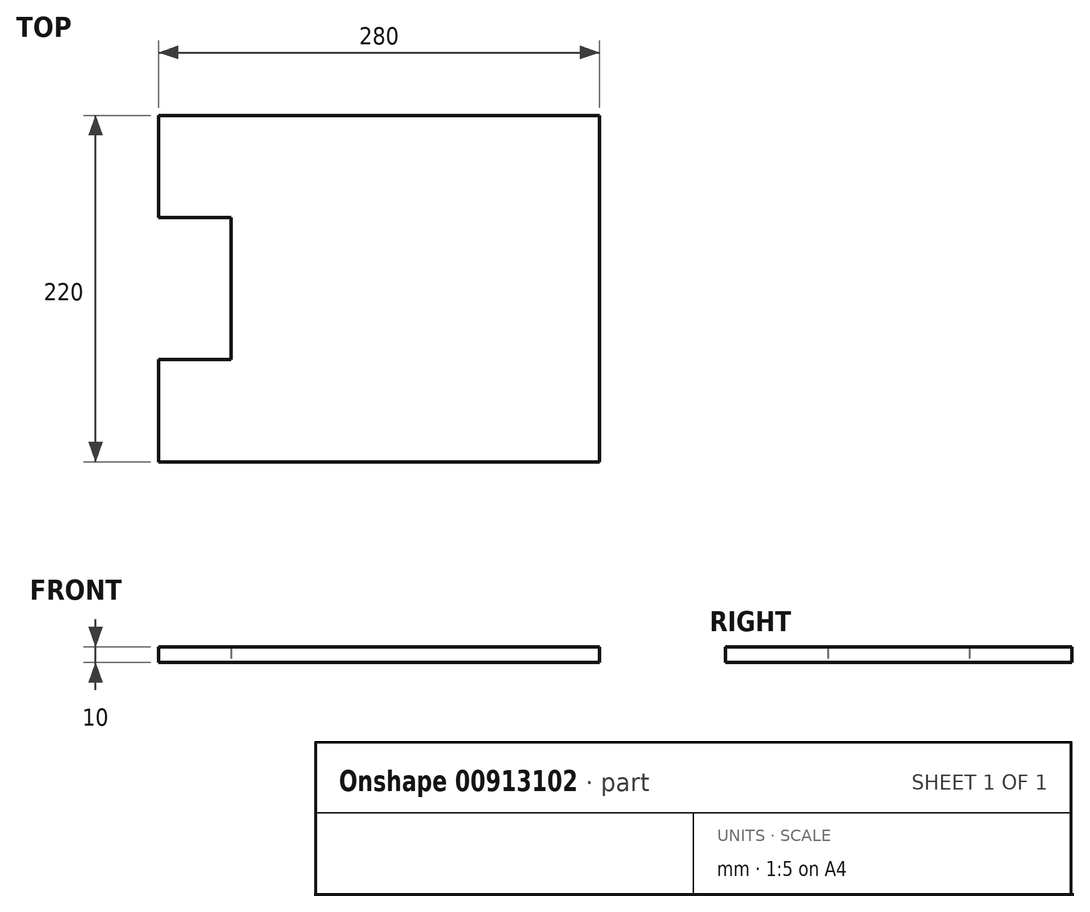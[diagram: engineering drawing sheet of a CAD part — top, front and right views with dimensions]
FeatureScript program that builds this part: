
annotation { "Feature Type Name" : "Feature", "Feature Type Description" : "" }
export const myFeature = defineFeature(function(context is Context, id is Id, definition is map)
    precondition{}
    {
        {
            var Q0;
            Q0=qCreatedBy(makeId("Top.planeOp"),FACE);
            var sketch = newSketch(context, id + "F0", { "sketchPlane" : qUnion([Q0])});
            skLineSegment(sketch, "E0.bottom", {"start": v(140, -110) * mm, "end": v(-140, -110) * mm});
            skLineSegment(sketch, "E0.top", {"start": v(140, 110) * mm, "end": v(-140, 110) * mm});
            skLineSegment(sketch, "E0.left", {"start": v(140, -110) * mm, "end": v(140, 110) * mm});
            skPoint(sketch, "E0.middle", {"position": v(0, 0) * mm});
            skLineSegment(sketch, "E1", {"start": v(-140, 110) * mm, "end": v(-140, 45) * mm});
            skLineSegment(sketch, "E2.MirrorCS", {"start": v(-140, -110) * mm, "end": v(-140, -45) * mm});
            skLineSegment(sketch, "E3", {"start": v(-140, 45) * mm, "end": v(-93.91, 45) * mm});
            skLineSegment(sketch, "E4.MirrorCS", {"start": v(-140, -45) * mm, "end": v(-93.91, -45) * mm});
            skLineSegment(sketch, "E5", {"start": v(-93.91, 45) * mm, "end": v(-93.91, -45) * mm});
            skSolve(sketch);
        }
        {
            var Q0;
            Q0 = qSketchRegion(id + "F0", true);
            extrude(context, id + "F1", {"entities" : qUnion([Q0]), "depth" : 10 * mm, "offsetDistance" : 25 * mm});
        }
    });
